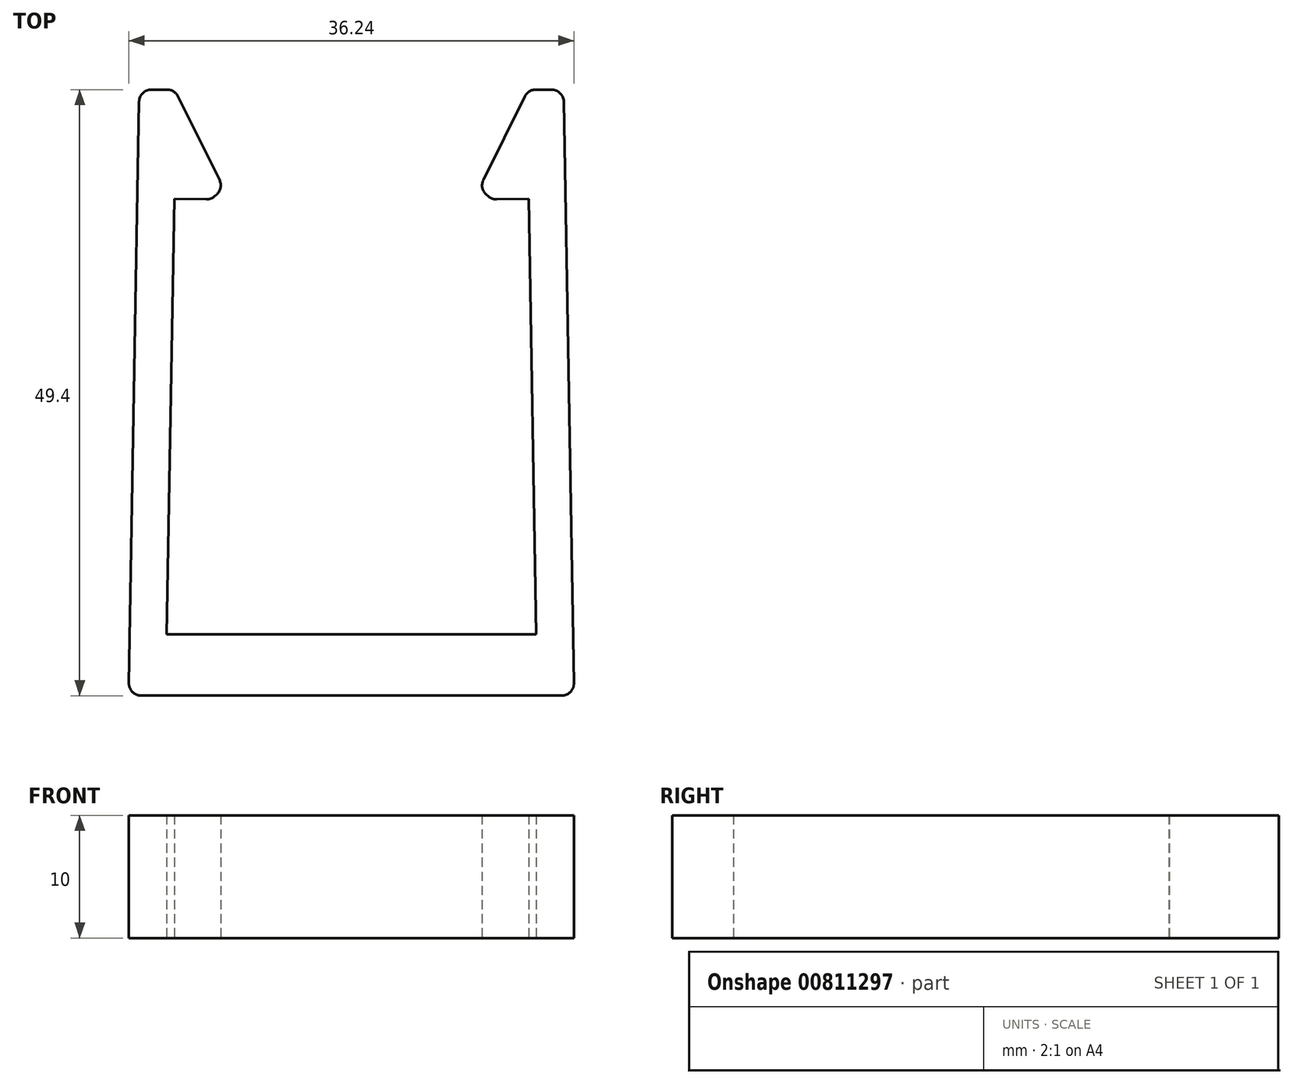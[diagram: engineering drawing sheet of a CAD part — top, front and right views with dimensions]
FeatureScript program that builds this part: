
annotation { "Feature Type Name" : "Feature", "Feature Type Description" : "" }
export const myFeature = defineFeature(function(context is Context, id is Id, definition is map)
    precondition{}
    {
        {
            var Q0;
            Q0=qCreatedBy(makeId("Top.planeOp"),FACE);
            var sketch = newSketch(context, id + "F0", { "sketchPlane" : qUnion([Q0])});
            skLineSegment(sketch, "E0", {"start": v(-15.05, -21.26) * mm, "end": v(-14.43, 14.24) * mm});
            skLineSegment(sketch, "E1", {"start": v(-14.43, 14.24) * mm, "end": v(-11.43, 14.18) * mm});
            skLineSegment(sketch, "E2", {"start": v(-11.43, 14.18) * mm, "end": v(-10.41, 15.11) * mm});
            skLineSegment(sketch, "E3", {"start": v(-10.41, 15.11) * mm, "end": v(-14.4, 23.14) * mm});
            skLineSegment(sketch, "E4", {"start": v(-14.4, 23.14) * mm, "end": v(-17.28, 23.14) * mm});
            skLineSegment(sketch, "E5", {"start": v(-17.28, 23.14) * mm, "end": v(-18.14, -26.26) * mm});
            skLineSegment(sketch, "E6.MirrorCS", {"start": v(11.43, 14.18) * mm, "end": v(10.41, 15.11) * mm});
            skLineSegment(sketch, "E7.MirrorCS", {"start": v(17.28, 23.14) * mm, "end": v(18.14, -26.26) * mm});
            skLineSegment(sketch, "E8.MirrorCS", {"start": v(14.4, 23.14) * mm, "end": v(17.28, 23.14) * mm});
            skLineSegment(sketch, "E9.MirrorCS", {"start": v(10.41, 15.11) * mm, "end": v(14.4, 23.14) * mm});
            skLineSegment(sketch, "E10.MirrorCS", {"start": v(14.43, 14.24) * mm, "end": v(11.43, 14.18) * mm});
            skLineSegment(sketch, "E11.MirrorCS", {"start": v(15.05, -21.26) * mm, "end": v(14.43, 14.24) * mm});
            skLineSegment(sketch, "E12", {"start": v(-15.05, -21.26) * mm, "end": v(15.05, -21.26) * mm});
            skLineSegment(sketch, "E13", {"start": v(-18.14, -26.26) * mm, "end": v(18.14, -26.26) * mm});
            skSolve(sketch);
        }
        {
            var Q0;
            Q0 = qSketchRegion(id + "F0", true);
            extrude(context, id + "F1", {"entities" : qUnion([Q0]), "depth" : 10 * mm, "offsetDistance" : 25 * mm});
        }
        {
            var Q0;
            Q0=makeQuery(id+"F1.opExtrude","SWEPT_EDGE",EDGE,{"disambiguationData":[OSD([sQuery(id+"F0.wireOp",EDGE,"E2"),sQuery(id+"F0.wireOp",EDGE,"E3")])]});
            var Q1;
            Q1=makeQuery(id+"F1.opExtrude","SWEPT_EDGE",EDGE,{"disambiguationData":[OSD([sQuery(id+"F0.wireOp",EDGE,"E6.MirrorCS"),sQuery(id+"F0.wireOp",EDGE,"E9.MirrorCS")])]});
            var Q2;
            Q2=makeQuery(id+"F1.opExtrude","SWEPT_EDGE",EDGE,{"disambiguationData":[OSD([sQuery(id+"F0.wireOp",EDGE,"E1"),sQuery(id+"F0.wireOp",EDGE,"E2")])]});
            var Q3;
            Q3=makeQuery(id+"F1.opExtrude","SWEPT_EDGE",EDGE,{"disambiguationData":[OSD([sQuery(id+"F0.wireOp",EDGE,"E6.MirrorCS"),sQuery(id+"F0.wireOp",EDGE,"E10.MirrorCS")])]});
            var Q4;
            Q4=makeQuery(id+"F1.opExtrude","SWEPT_EDGE",EDGE,{"disambiguationData":[OSD([sQuery(id+"F0.wireOp",EDGE,"E4"),sQuery(id+"F0.wireOp",EDGE,"E5")])]});
            var Q5;
            Q5=makeQuery(id+"F1.opExtrude","SWEPT_EDGE",EDGE,{"disambiguationData":[OSD([sQuery(id+"F0.wireOp",EDGE,"E3"),sQuery(id+"F0.wireOp",EDGE,"E4")])]});
            var Q6;
            Q6=makeQuery(id+"F1.opExtrude","SWEPT_EDGE",EDGE,{"disambiguationData":[OSD([sQuery(id+"F0.wireOp",EDGE,"E5"),sQuery(id+"F0.wireOp",EDGE,"E13")])]});
            var Q7;
            Q7=makeQuery(id+"F1.opExtrude","SWEPT_EDGE",EDGE,{"disambiguationData":[OSD([sQuery(id+"F0.wireOp",EDGE,"E7.MirrorCS"),sQuery(id+"F0.wireOp",EDGE,"E13")])]});
            var Q8;
            Q8=makeQuery(id+"F1.opExtrude","SWEPT_EDGE",EDGE,{"disambiguationData":[OSD([sQuery(id+"F0.wireOp",EDGE,"E7.MirrorCS"),sQuery(id+"F0.wireOp",EDGE,"E8.MirrorCS")])]});
            var Q9;
            Q9=makeQuery(id+"F1.opExtrude","SWEPT_EDGE",EDGE,{"disambiguationData":[OSD([sQuery(id+"F0.wireOp",EDGE,"E8.MirrorCS"),sQuery(id+"F0.wireOp",EDGE,"E9.MirrorCS")])]});
            fillet(context, id + "F2", {"entities" : qUnion([Q0, Q1, Q2, Q3, Q4, Q5, Q6, Q7, Q8, Q9]), "radius" : 1 * mm, "tangentPropagation" : true, "allowEdgeOverflow" : false});
        }
    });
